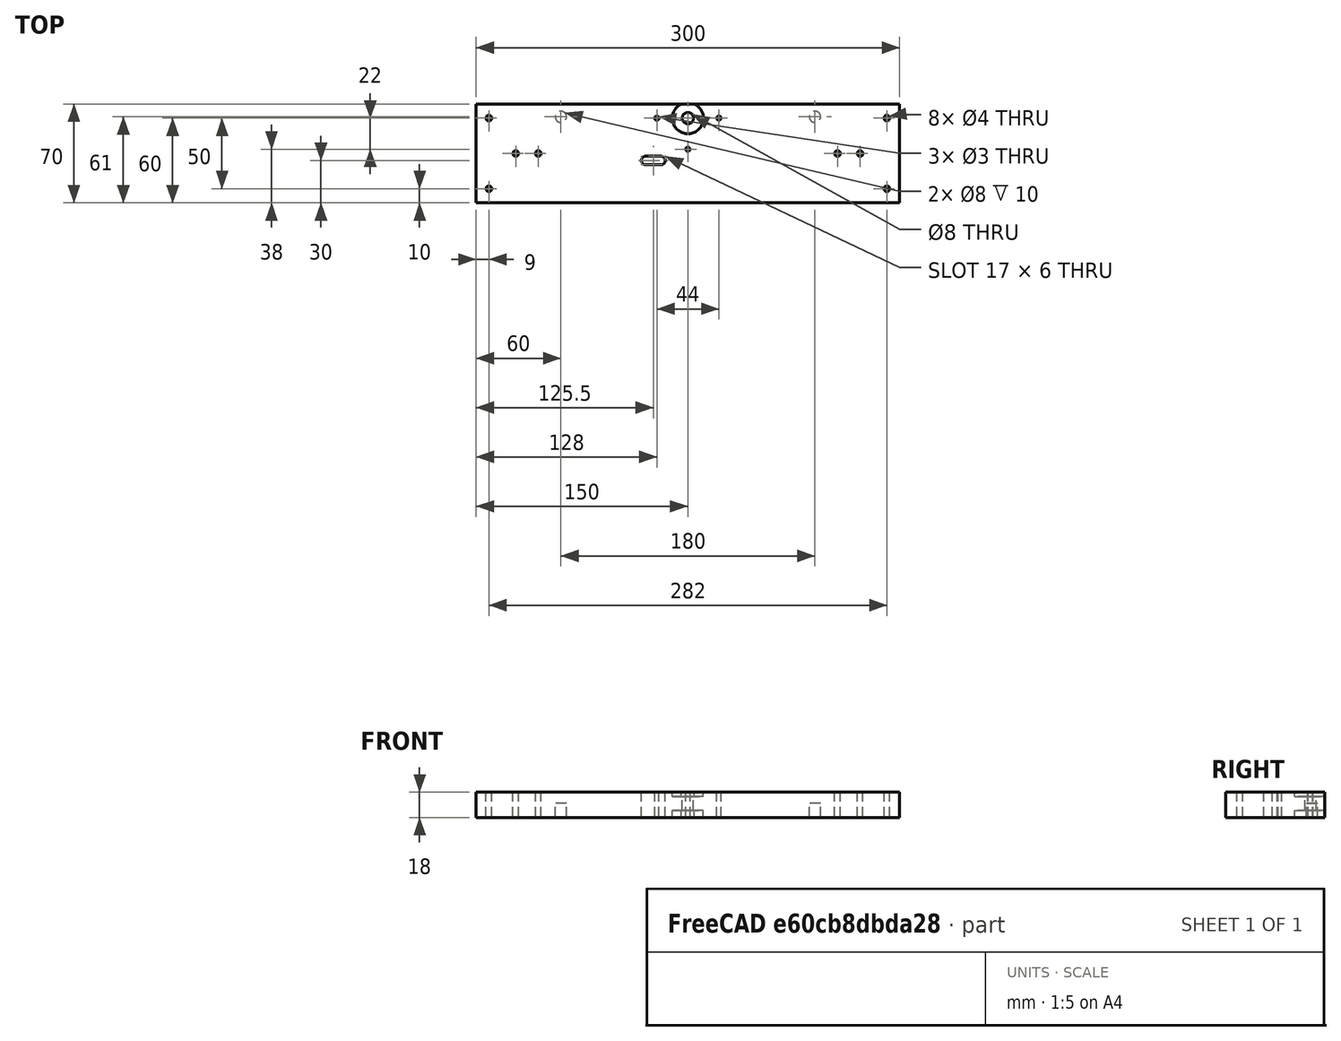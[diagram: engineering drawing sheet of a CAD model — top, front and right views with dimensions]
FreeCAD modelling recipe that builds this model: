
FCSTD DOCUMENT  (FreeCAD 0.17R13541 (Git))
Label: Base-Delante
License: All rights reserved
LicenseURL: http://en.wikipedia.org/wiki/All_rights_reserved
objects: Part::Cylinder×10, Part::Cut×7, Part::MultiFuse×4, Part::FeaturePython×3, Part::Box×2, Part::Mirroring×1
note: 27 computed .brp shape members not serialized (recipe doc carries the construction recipe); baked Part::Feature solids carry a one-line shape summary decoded from their .brp

FEATURE [Part::Box] Box  label="Cubo"
  AttacherType = Attacher::AttachEngine3D
  Height = 18
  Length = 150
  Width = 70
FEATURE [Part::Cylinder] Cylinder  label="Cilindro"
  Angle = 360
  AttacherType = Attacher::AttachEngine3D
  Height = 25
  Radius = 2
FEATURE [Part::FeaturePython] Array  # Draft array (typed FeaturePython)
  Angle = 360
  ArrayType = 0
  Axis = (0,0,1)
  Base = -> Cylinder
  Center = (0,0,0)
  Fuse = false
  IntervalAxis = (0,0,0)
  IntervalX = (1,0,0)
  IntervalY = (0,50,0)
  IntervalZ = (0,0,0)
  NumberPolar = 1
  NumberX = 1
  NumberY = 2
  NumberZ = 1
  Placement = pos=(9,10,0) rot=(0,0,1;0rad)
FEATURE [Part::Cylinder] Cylinder001  label="Cilindro001"
  Angle = 360
  AttacherType = Attacher::AttachEngine3D
  Height = 25
  Placement = pos=(28,0,0) rot=(0,0,1;0rad)
  Radius = 2
FEATURE [Part::FeaturePython] Array001  # Draft array (typed FeaturePython)
  Angle = 360
  ArrayType = 0
  Axis = (0,0,1)
  Base = -> Cylinder001
  Center = (0,0,0)
  Fuse = false
  IntervalAxis = (0,0,0)
  IntervalX = (16,0,0)
  IntervalY = (0,0,0)
  IntervalZ = (0,0,0)
  NumberPolar = 1
  NumberX = 2
  NumberY = 1
  NumberZ = 1
  Placement = pos=(0,35,0) rot=(0,0,1;0rad)
FEATURE [Part::Cylinder] Cylinder002  label="Cilindro002"
  Angle = 360
  AttacherType = Attacher::AttachEngine3D
  Height = 25
  Placement = pos=(22,0,0) rot=(0,0,1;0rad)
  Radius = 1.5
FEATURE [Part::FeaturePython] Array002  # Draft array (typed FeaturePython)
  Angle = 360
  ArrayType = 1
  Axis = (0,0,1)
  Base = -> Cylinder002
  Center = (0,0,0)
  Fuse = false
  IntervalAxis = (0,0,0)
  IntervalX = (1,0,0)
  IntervalY = (0,1,0)
  IntervalZ = (0,0,0)
  NumberPolar = 4
  NumberX = 2
  NumberY = 2
  NumberZ = 1
  Placement = pos=(150,60,0) rot=(0,0,1;0rad)
FEATURE [Part::Cut] Cut
  Base = -> Box
  Refine = true
  Tool = -> Array001
FEATURE [Part::Cut] Cut001  label="Base"
  Base = -> Cut
  Refine = true
  Tool = -> Array
FEATURE [Part::Cylinder] Cylinder003  label="Cilindro003"
  Angle = 360
  AttacherType = Attacher::AttachEngine3D
  Height = 10
  Placement = pos=(0,0,15) rot=(0,0,1;0rad)
  Radius = 11
FEATURE [Part::Cylinder] Cylinder004  label="Cilindro004"
  Angle = 360
  AttacherType = Attacher::AttachEngine3D
  Height = 30
  Placement = pos=(150,60,0) rot=(0,0,1;0rad)
  Radius = 4
FEATURE [Part::Cylinder] Cylinder005  label="Cilindro005"
  Angle = 360
  AttacherType = Attacher::AttachEngine3D
  Height = 5
  Radius = 11
FEATURE [Part::MultiFuse] Fusion
  Placement = pos=(150,60,0) rot=(0,0,1;0rad)
  Refine = true
  Shapes = -> [Cylinder005,Cylinder003]
FEATURE [Part::MultiFuse] Fusion001  label="HuecoMotor"
  Refine = true
  Shapes = -> [Cylinder004,Fusion]
FEATURE [Part::Mirroring] mirror  label="Mirror of Base"
  Base = (150,0,0)
  Normal = (-0.51,0,0)
  Source = -> Cut001
FEATURE [Part::Cylinder] Cylinder006  label="Cilindro006"
  Angle = 360
  AttacherType = Attacher::AttachEngine3D
  Height = 25
  Placement = pos=(120,30,0) rot=(0,0,1;0rad)
  Radius = 3
FEATURE [Part::Box] Box001  label="Cubo001"
  AttacherType = Attacher::AttachEngine3D
  Height = 25
  Length = 11
  Placement = pos=(120,27,0) rot=(0,0,1;0rad)
  Width = 6
FEATURE [Part::Cylinder] Cylinder007  label="Cilindro007"
  Angle = 360
  AttacherType = Attacher::AttachEngine3D
  Height = 25
  Placement = pos=(131,30,0) rot=(0,0,1;0rad)
  Radius = 3
FEATURE [Part::MultiFuse] Fusion002
  Refine = true
  Shapes = -> [Cylinder007,Box001,Cylinder006]
FEATURE [Part::Cut] Cut002
  Base = -> Cut001
  Refine = true
  Tool = -> Fusion002
FEATURE [Part::MultiFuse] Fusion003
  Refine = true
  Shapes = -> [Cut002,mirror]
FEATURE [Part::Cut] Cut003
  Base = -> Fusion003
  Refine = true
  Tool = -> Fusion001
FEATURE [Part::Cut] Cut004
  Base = -> Cut003
  Refine = true
  Tool = -> Array002
FEATURE [Part::Cylinder] Cylinder008  label="Cilindro008"
  Angle = 360
  AttacherType = Attacher::AttachEngine3D
  Height = 10
  Placement = pos=(60,61,0) rot=(0,0,1;0rad)
  Radius = 4
FEATURE [Part::Cylinder] Cylinder009  label="Cilindro009"
  Angle = 360
  AttacherType = Attacher::AttachEngine3D
  Height = 10
  Placement = pos=(240,61,0) rot=(0,0,1;0rad)
  Radius = 4
FEATURE [Part::Cut] Cut005
  Base = -> Cut004
  Refine = true
  Tool = -> Cylinder008
FEATURE [Part::Cut] Cut006
  Base = -> Cut005
  Refine = true
  Tool = -> Cylinder009
